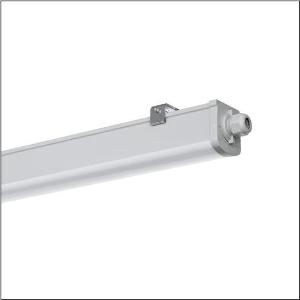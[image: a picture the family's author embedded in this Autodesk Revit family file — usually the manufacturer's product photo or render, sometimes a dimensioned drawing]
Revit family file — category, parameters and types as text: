
# Revit family: monsun_r__31_51fa207k430b_6f38
name_source: partatom
category: Lighting Fixtures
units: mm (PartAtom-declared; Revit-internal decimal feet)

## family parameters
Cut with Voids When Loaded = No
Host = Face
Light Source = No
Part Type = Normal
Room Calculation Point = No
Round Connector Dimension = Use Diameter
Shared = No

## types (1)
- Monsun® 31 (1 x LED, 3000 lm, 22 W, 4000K)
    Apparent Load = 22 VA
    CIE Flux Codes = 42 72 91 92 100
    Color Rendering = 80
    Color Temperature = 4000K
    Default Elevation = 1800 mm
    Description = Monsun® 31, damp-proof luminaire, primary optical cover: diffuser, of PC, frosted, light emission: direct distribution, primary light characteristic: symmetric, installation type: surface-mounted, LED, rated luminous flux: 3.000lm, luminous efficacy: 136lm/W, light colour: 840, colour temperature: 4000K, control gear: ECG, with terminal, 3+1-pole, max. 2.5mm², through-wiring: 3x 2.5mm² + 1x 1.5mm², mains connection: 220..240V, AC, 50/60Hz, rated input power: 22W, housing, luminaire housing, of PC, light grey (RAL 7035), length: 1.158mm, width: 68mm, height: 76mm, protection rating (complete): IP66, insulation class (complete): insulation class II (safety insulation), certification: CE, ENEC, UKCA, protection symbol: D, impact resistance: IK08, permissible operating ambient temperature: -20..+40°C, corresponds to IFS (International Featured Standards) requirements for safety and quality in the food industry, contact your sales advisor before using the luminaires in applications with unclear chemical exposure, large temperature fluctuations or condensation-forming humidity, packaging unit: 1 piece
    Height = 77 mm
    Lamp = 1 x LED
    Lamp Light Flux = 3000 lm
    Lamp Power = 22 W
    Lamp count = 1
    Length = 1218 mm
    Luminous efficacy = 136 lm/W
    Manufacturer = Siteco
    ModVariant = No
    Model = 51FA207K430B
    Mounting Place = Ceiling
    Mounting Type = Surface mounted
    Number of Poles = 1
    OnlyDefault = Yes
    Power Factor = 1
    Product Name = Monsun® 31
    Product group = damp-proof luminaire
    ProductGroupID = 301
    Protection Class = Protection class II
    Protection Degree = IP 66
    RLX_Detail_Level = 1
    RLX_Emergency_Light_Flux = 0 lm
    RLX_Emergency_Type = 0
    RLX_Emergency_Type_DB = No
    RlxData = <blob elided: 32849 chars, md5=d3369060>
    Socket = socket
    Standby Power = 0 W
    System Light Flux = 3000 lm
    System Power = 22 W
    Type Comments = Product without accessories
    Type Image = l_1006174.jpg
    URL = http://relux.com
    VarID = ---
    Voltage = 0 V
    Weight = 0.00 kg
    Width = 69 mm

## geometry (parser evidence)
native form markers: Blend x4, Sweep x12
no freeform markers — native parametric forms only
